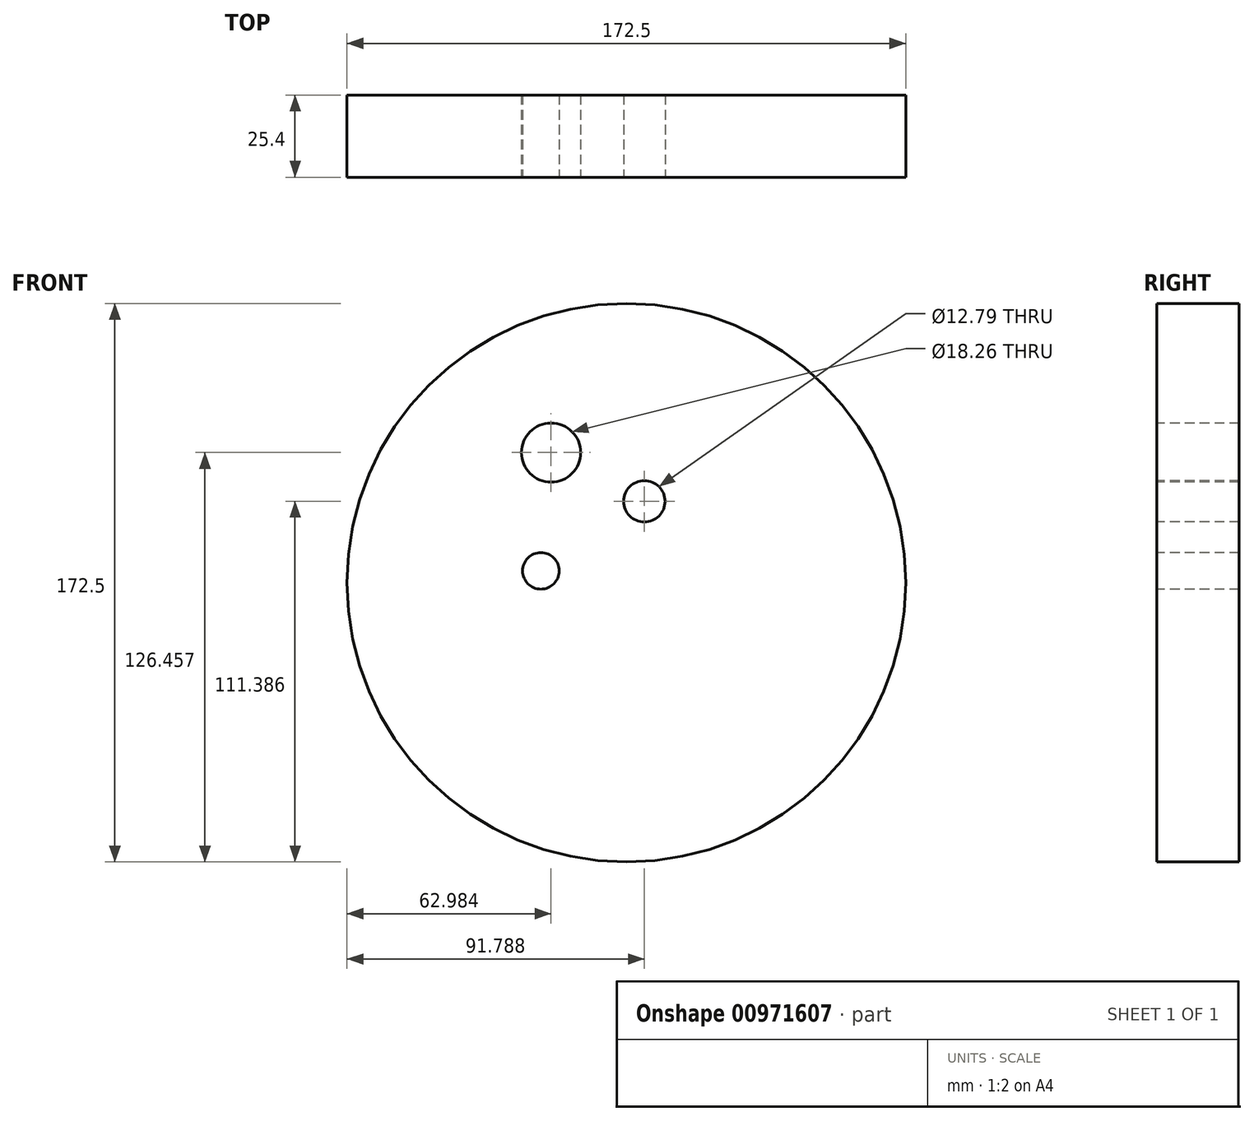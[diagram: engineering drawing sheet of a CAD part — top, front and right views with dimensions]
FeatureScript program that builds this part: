
annotation { "Feature Type Name" : "Feature", "Feature Type Description" : "" }
export const myFeature = defineFeature(function(context is Context, id is Id, definition is map)
    precondition{}
    {
        {
            var Q0;
            Q0=qCreatedBy(makeId("Front.planeOp"),FACE);
            var sketch = newSketch(context, id + "F0", { "sketchPlane" : qUnion([Q0])});
            skCircle(sketch, "E0", {"center": v(0, 0) * mm, "radius": 86.25 * mm});
            skSolve(sketch);
        }
        {
            var Q0;
            Q0=makeQuery(id+"F0.imprint","IMPRINT",FACE,{"disambiguationData":[TD([[makeQuery(id+"F0.imprint","IMPRINT",EDGE,{"derivedFrom":sQuery(id+"F0.wireOp",EDGE,"E0")}),1.0]])]});
            extrude(context, id + "F1", {"entities" : qUnion([Q0]), "depth" : 25.4 * mm, "offsetDistance" : 25.4 * mm});
        }
        {
            var Q0;
            Q0=makeQuery(id+"F1.opExtrude","CAP_FACE",FACE,{"disambiguationData":[OSD([sQuery(id+"F0.wireOp",EDGE,"E0")])],"isStart":false});
            var sketch = newSketch(context, id + "F2", { "sketchPlane" : qUnion([Q0])});
            skCircle(sketch, "E1", {"center": v(-26.4, 3.65) * mm, "radius": 5.64 * mm});
            skCircle(sketch, "E2", {"center": v(-23.27, 40.2) * mm, "radius": 9.13 * mm});
            skCircle(sketch, "E3", {"center": v(5.54, 25.14) * mm, "radius": 6.4 * mm});
            skSolve(sketch);
        }
        {
            var Q0;
            Q0 = qSketchRegion(id + "F2", true);
            extrude(context, id + "F3", {"entities" : qUnion([Q0]), "operationType" : NewBodyOperationType.REMOVE, "endBound" : BoundingType.THROUGH_ALL, "oppositeDirection" : true, "depth" : 25.4 * mm, "offsetDistance" : 25.4 * mm});
        }
    });
